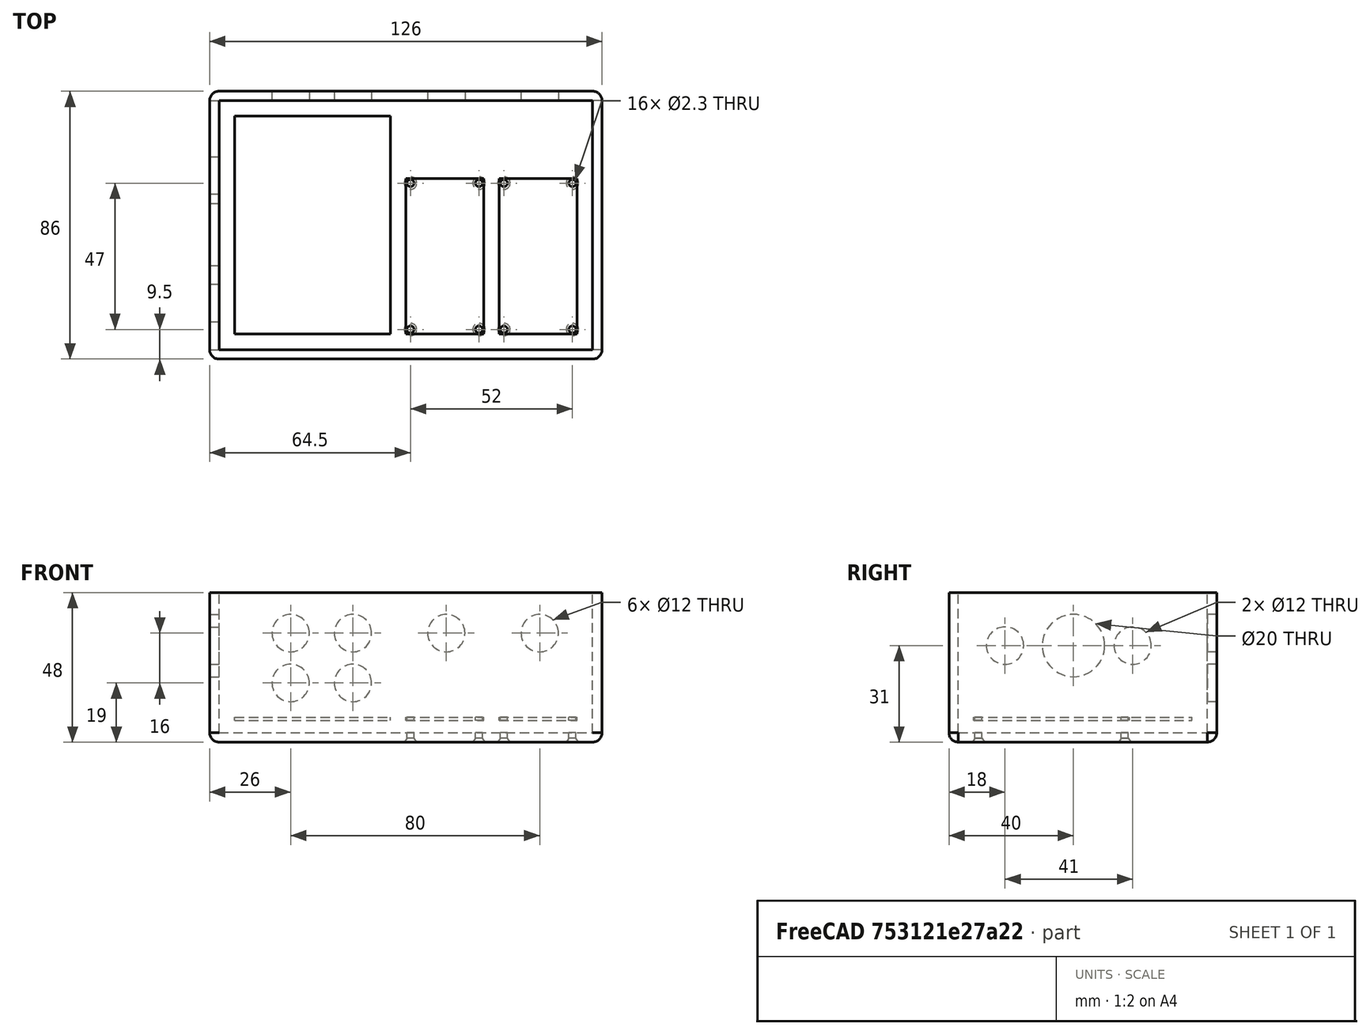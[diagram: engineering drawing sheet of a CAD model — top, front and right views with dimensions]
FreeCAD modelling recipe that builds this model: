
FCSTD DOCUMENT  (FreeCAD 0.17R13541 (Git))
Label: Boitier
License: All rights reserved
LicenseURL: http://en.wikipedia.org/wiki/All_rights_reserved
objects: Part::MultiFuse×23, Part::Cylinder×17, Part::Cone×8, Part::Box×4, Part::Cut×2, Part::Thickness×1
note: 55 computed .brp shape members not serialized (recipe doc carries the construction recipe); baked Part::Feature solids carry a one-line shape summary decoded from their .brp

FEATURE [Part::Box] Box  label="Cube"
  AttacherType = Attacher::AttachEngine3D
  Height = 45
  Length = 120
  Width = 80
FEATURE [Part::Thickness] Thickness  label="Boîte"
  Faces = -> Box [Face6]
  Intersection = false
  Join = 0
  Mode = 0
  SelfIntersection = false
  Value = 3
FEATURE [Part::Box] Box001  label="Carte"
  AttacherType = Attacher::AttachEngine3D
  Height = 1
  Length = 25
  Placement = pos=(90,5,4) rot=(0,0,1;0rad)
  Width = 50
FEATURE [Part::Box] Box002  label="Carte001"
  AttacherType = Attacher::AttachEngine3D
  Height = 1
  Length = 25
  Placement = pos=(60,5,4) rot=(0,0,1;0rad)
  Width = 50
FEATURE [Part::Cylinder] Cylinder  label="Cylindre"
  Angle = 360
  AttacherType = Attacher::AttachEngine3D
  Height = 20
  Radius = 6
FEATURE [Part::Cylinder] Cylinder001  label="Cylindre001"
  Angle = 360
  AttacherType = Attacher::AttachEngine3D
  Height = 20
  Placement = pos=(16,0,0) rot=(0,0,1;0rad)
  Radius = 6
FEATURE [Part::Cylinder] Cylinder002  label="Cylindre002"
  Angle = 360
  AttacherType = Attacher::AttachEngine3D
  Height = 20
  Placement = pos=(16,-16,0) rot=(0,0,1;0rad)
  Radius = 6
FEATURE [Part::Cylinder] Cylinder003  label="Cylindre003"
  Angle = 360
  AttacherType = Attacher::AttachEngine3D
  Height = 20
  Placement = pos=(0,-16,0) rot=(0,0,1;0rad)
  Radius = 6
FEATURE [Part::Cylinder] Cylinder004  label="Cylindre004"
  Angle = 360
  AttacherType = Attacher::AttachEngine3D
  Height = 20
  Placement = pos=(73,-8,0) rot=(0,0,1;0rad)
  Radius = 6
FEATURE [Part::Cylinder] Cylinder005  label="Cylindre005"
  Angle = 360
  AttacherType = Attacher::AttachEngine3D
  Height = 20
  Placement = pos=(103,-8,0) rot=(0,0,1;0rad)
  Radius = 6
FEATURE [Part::MultiFuse] Fusion
  Placement = pos=(27,0,0) rot=(0,0,1;0rad)
  Shapes = -> [Cylinder001,Cylinder002]
FEATURE [Part::MultiFuse] Fusion001
  Placement = pos=(23,0,0) rot=(0,0,1;0rad)
  Shapes = -> [Cylinder,Cylinder003]
FEATURE [Part::MultiFuse] Fusion002
  Placement = pos=(0,15,0) rot=(0,0,1;0rad)
  Shapes = -> [Cylinder004,Cylinder005]
FEATURE [Part::Cylinder] Cylinder006  label="Cylindre006"
  Angle = 360
  AttacherType = Attacher::AttachEngine3D
  Height = 30
  Placement = pos=(-4,15,20) rot=(0,1,0;1.5708rad)
  Radius = 6
FEATURE [Part::Cylinder] Cylinder007  label="Cylindre007"
  Angle = 360
  AttacherType = Attacher::AttachEngine3D
  Height = 20
  Placement = pos=(-4,56,20) rot=(0,1,0;1.5708rad)
  Radius = 6
FEATURE [Part::Cylinder] Cylinder008  label="Cylindre008"
  Angle = 360
  AttacherType = Attacher::AttachEngine3D
  Height = 20
  Placement = pos=(-4,37,20) rot=(0,1,0;1.5708rad)
  Radius = 10
FEATURE [Part::MultiFuse] Fusion004
  Shapes = -> [Thickness,Box001,Box002]
FEATURE [Part::MultiFuse] Fusion005
  Placement = pos=(0,0,8) rot=(0,0,1;0rad)
  Shapes = -> [Cylinder006,Cylinder007,Cylinder008]
FEATURE [Part::Cylinder] Cylinder010  label="Cylindre010"
  Angle = 360
  AttacherType = Attacher::AttachEngine3D
  Height = 15
  Placement = pos=(0,0,1) rot=(0,0,1;0rad)
  Radius = 1.15
FEATURE [Part::Cone] Cone  label="Cône"
  Angle = 360
  AttacherType = Attacher::AttachEngine3D
  Height = 1.3
  Radius1 = 2
  Radius2 = 1.15
FEATURE [Part::MultiFuse] Fusion006  label="Vis"
  Shapes = -> [Cylinder010,Cone]
FEATURE [Part::Cylinder] Cylinder011  label="Cylindre011"
  Angle = 360
  AttacherType = Attacher::AttachEngine3D
  Height = 15
  Placement = pos=(0,0,1) rot=(0,0,1;0rad)
  Radius = 1.15
FEATURE [Part::Cone] Cone001  label="Cône001"
  Angle = 360
  AttacherType = Attacher::AttachEngine3D
  Height = 1.3
  Radius1 = 2
  Radius2 = 1.15
FEATURE [Part::MultiFuse] Fusion007  label="Vis001"
  Placement = pos=(22,0,0) rot=(0,0,1;0rad)
  Shapes = -> [Cylinder011,Cone001]
FEATURE [Part::MultiFuse] Fusion008
  Shapes = -> [Fusion006,Fusion007]
FEATURE [Part::Cylinder] Cylinder012  label="Cylindre012"
  Angle = 360
  AttacherType = Attacher::AttachEngine3D
  Height = 15
  Placement = pos=(0,0,1) rot=(0,0,1;0rad)
  Radius = 1.15
FEATURE [Part::Cone] Cone002  label="Cône002"
  Angle = 360
  AttacherType = Attacher::AttachEngine3D
  Height = 1.3
  Radius1 = 2
  Radius2 = 1.15
FEATURE [Part::MultiFuse] Fusion010  label="Vis002"
  Shapes = -> [Cylinder012,Cone002]
FEATURE [Part::Cylinder] Cylinder013  label="Cylindre013"
  Angle = 360
  AttacherType = Attacher::AttachEngine3D
  Height = 15
  Placement = pos=(0,0,1) rot=(0,0,1;0rad)
  Radius = 1.15
FEATURE [Part::Cone] Cone003  label="Cône003"
  Angle = 360
  AttacherType = Attacher::AttachEngine3D
  Height = 1.3
  Radius1 = 2
  Radius2 = 1.15
FEATURE [Part::MultiFuse] Fusion011  label="Vis003"
  Placement = pos=(22,0,0) rot=(0,0,1;0rad)
  Shapes = -> [Cylinder013,Cone003]
FEATURE [Part::MultiFuse] Fusion009
  Placement = pos=(0,-47,0) rot=(0,0,1;0rad)
  Shapes = -> [Fusion010,Fusion011]
FEATURE [Part::MultiFuse] Fusion012  label="Vis cartes alim"
  Placement = pos=(61.5,53.5,-3) rot=(0,0,1;0rad)
  Shapes = -> [Fusion008,Fusion009]
FEATURE [Part::Cone] Cone004  label="Cône004"
  Angle = 360
  AttacherType = Attacher::AttachEngine3D
  Height = 1.3
  Radius1 = 2
  Radius2 = 1.15
FEATURE [Part::Cylinder] Cylinder014  label="Cylindre014"
  Angle = 360
  AttacherType = Attacher::AttachEngine3D
  Height = 15
  Placement = pos=(0,0,1) rot=(0,0,1;0rad)
  Radius = 1.15
FEATURE [Part::Cylinder] Cylinder015  label="Cylindre015"
  Angle = 360
  AttacherType = Attacher::AttachEngine3D
  Height = 15
  Placement = pos=(0,0,1) rot=(0,0,1;0rad)
  Radius = 1.15
FEATURE [Part::Cone] Cone005  label="Cône005"
  Angle = 360
  AttacherType = Attacher::AttachEngine3D
  Height = 1.3
  Radius1 = 2
  Radius2 = 1.15
FEATURE [Part::MultiFuse] Fusion015  label="Vis004"
  Shapes = -> [Cylinder015,Cone005]
FEATURE [Part::Cone] Cone006  label="Cône006"
  Angle = 360
  AttacherType = Attacher::AttachEngine3D
  Height = 1.3
  Radius1 = 2
  Radius2 = 1.15
FEATURE [Part::Cylinder] Cylinder016  label="Cylindre016"
  Angle = 360
  AttacherType = Attacher::AttachEngine3D
  Height = 15
  Placement = pos=(0,0,1) rot=(0,0,1;0rad)
  Radius = 1.15
FEATURE [Part::MultiFuse] Fusion016  label="Vis005"
  Shapes = -> [Cylinder016,Cone006]
FEATURE [Part::Cylinder] Cylinder017  label="Cylindre017"
  Angle = 360
  AttacherType = Attacher::AttachEngine3D
  Height = 15
  Placement = pos=(0,0,1) rot=(0,0,1;0rad)
  Radius = 1.15
FEATURE [Part::MultiFuse] Fusion017  label="Vis006"
  Placement = pos=(22,0,0) rot=(0,0,1;0rad)
  Shapes = -> [Cylinder014,Cone004]
FEATURE [Part::MultiFuse] Fusion013
  Placement = pos=(0,-47,0) rot=(0,0,1;0rad)
  Shapes = -> [Fusion016,Fusion017]
FEATURE [Part::Cone] Cone007  label="Cône007"
  Angle = 360
  AttacherType = Attacher::AttachEngine3D
  Height = 1.3
  Radius1 = 2
  Radius2 = 1.15
FEATURE [Part::MultiFuse] Fusion018  label="Vis007"
  Placement = pos=(22,0,0) rot=(0,0,1;0rad)
  Shapes = -> [Cylinder017,Cone007]
FEATURE [Part::MultiFuse] Fusion014
  Shapes = -> [Fusion015,Fusion018]
FEATURE [Part::MultiFuse] Fusion019  label="Vis cartes alim001"
  Placement = pos=(91.5,53.5,-3) rot=(0,0,1;0rad)
  Shapes = -> [Fusion014,Fusion013]
FEATURE [Part::MultiFuse] Fusion020
  Shapes = -> [Fusion019,Fusion012]
FEATURE [Part::Cut] Cut
  Base = -> Fusion004
  Tool = -> Fusion020
FEATURE [Part::Box] Box003  label="Cube001"
  AttacherType = Attacher::AttachEngine3D
  Height = 1
  Length = 50
  Placement = pos=(5,5,4) rot=(0,0,1;0rad)
  Width = 70
FEATURE [Part::MultiFuse] Fusion021
  Placement = pos=(0,7,0) rot=(0,0,1;0rad)
  Shapes = -> [Fusion001,Fusion]
FEATURE [Part::MultiFuse] Fusion022
  Placement = pos=(0,91.5,25) rot=(1,0,0;1.5708rad)
  Shapes = -> [Fusion002,Fusion021]
FEATURE [Part::MultiFuse] Fusion023
  Shapes = -> [Fusion005,Fusion022]
FEATURE [Part::Cut] Cut001
  Base = -> Cut
  Tool = -> Fusion023
